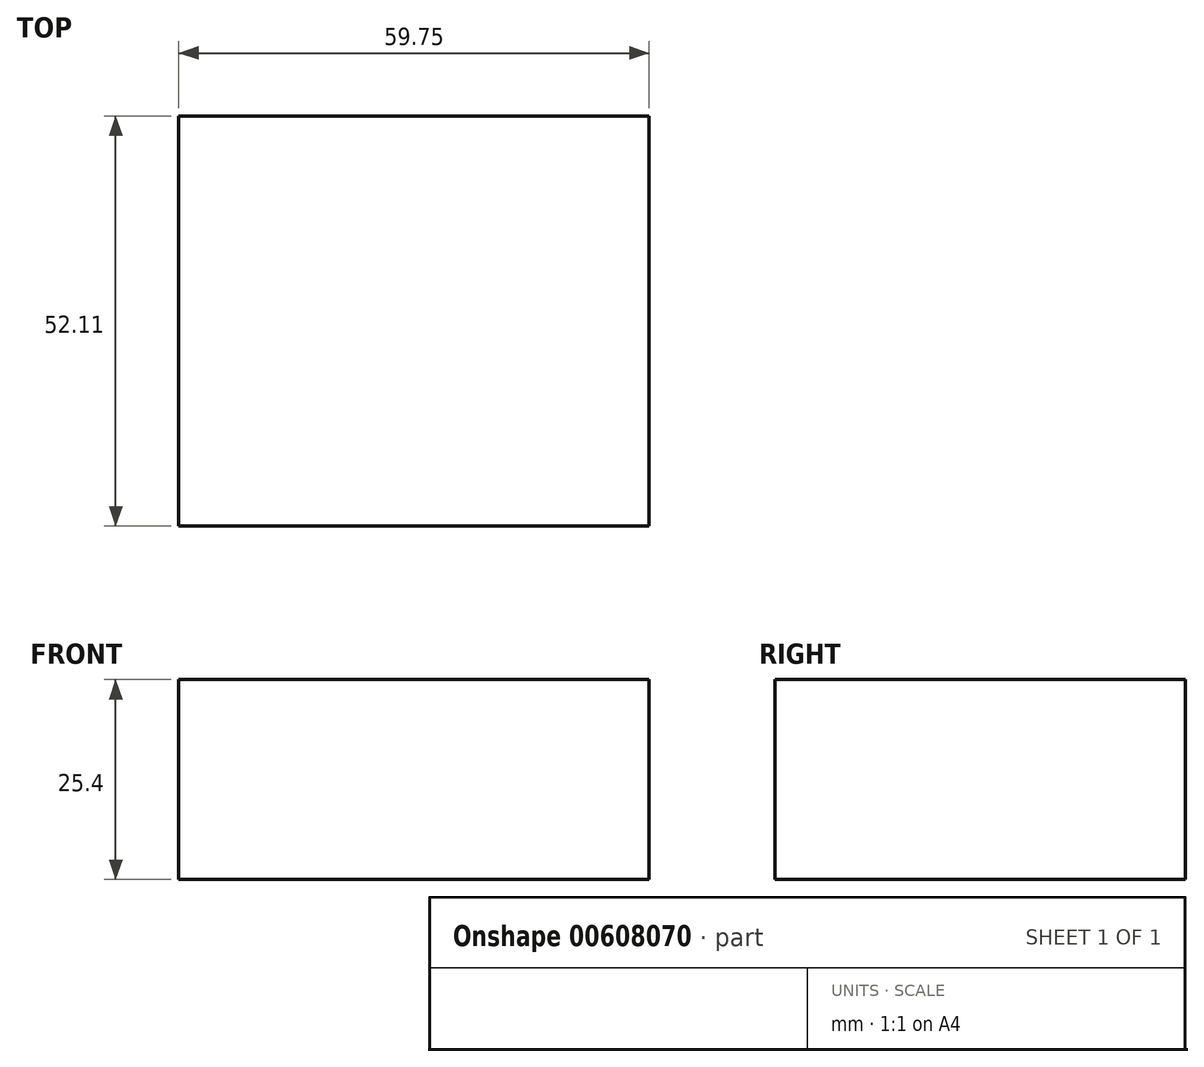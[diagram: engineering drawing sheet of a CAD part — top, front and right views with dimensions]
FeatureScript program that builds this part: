
annotation { "Feature Type Name" : "Feature", "Feature Type Description" : "" }
export const myFeature = defineFeature(function(context is Context, id is Id, definition is map)
    precondition{}
    {
        {
            var Q0;
            Q0=qCreatedBy(makeId("Top.planeOp"),FACE);
            var sketch = newSketch(context, id + "F0", { "sketchPlane" : qUnion([Q0])});
            skLineSegment(sketch, "E0.bottom", {"start": v(0, 0) * mm, "end": v(59.75, 0) * mm});
            skLineSegment(sketch, "E0.top", {"start": v(0, 52.1) * mm, "end": v(59.75, 52.1) * mm});
            skLineSegment(sketch, "E0.left", {"start": v(0, 0) * mm, "end": v(0, 52.1) * mm});
            skLineSegment(sketch, "E0.right", {"start": v(59.75, 0) * mm, "end": v(59.75, 52.1) * mm});
            skSolve(sketch);
        }
        {
            var Q0;
            Q0 = qSketchRegion(id + "F0", true);
            extrude(context, id + "F1", {"entities" : qUnion([Q0]), "depth" : 25.4 * mm, "offsetDistance" : 25.4 * mm});
        }
    });
